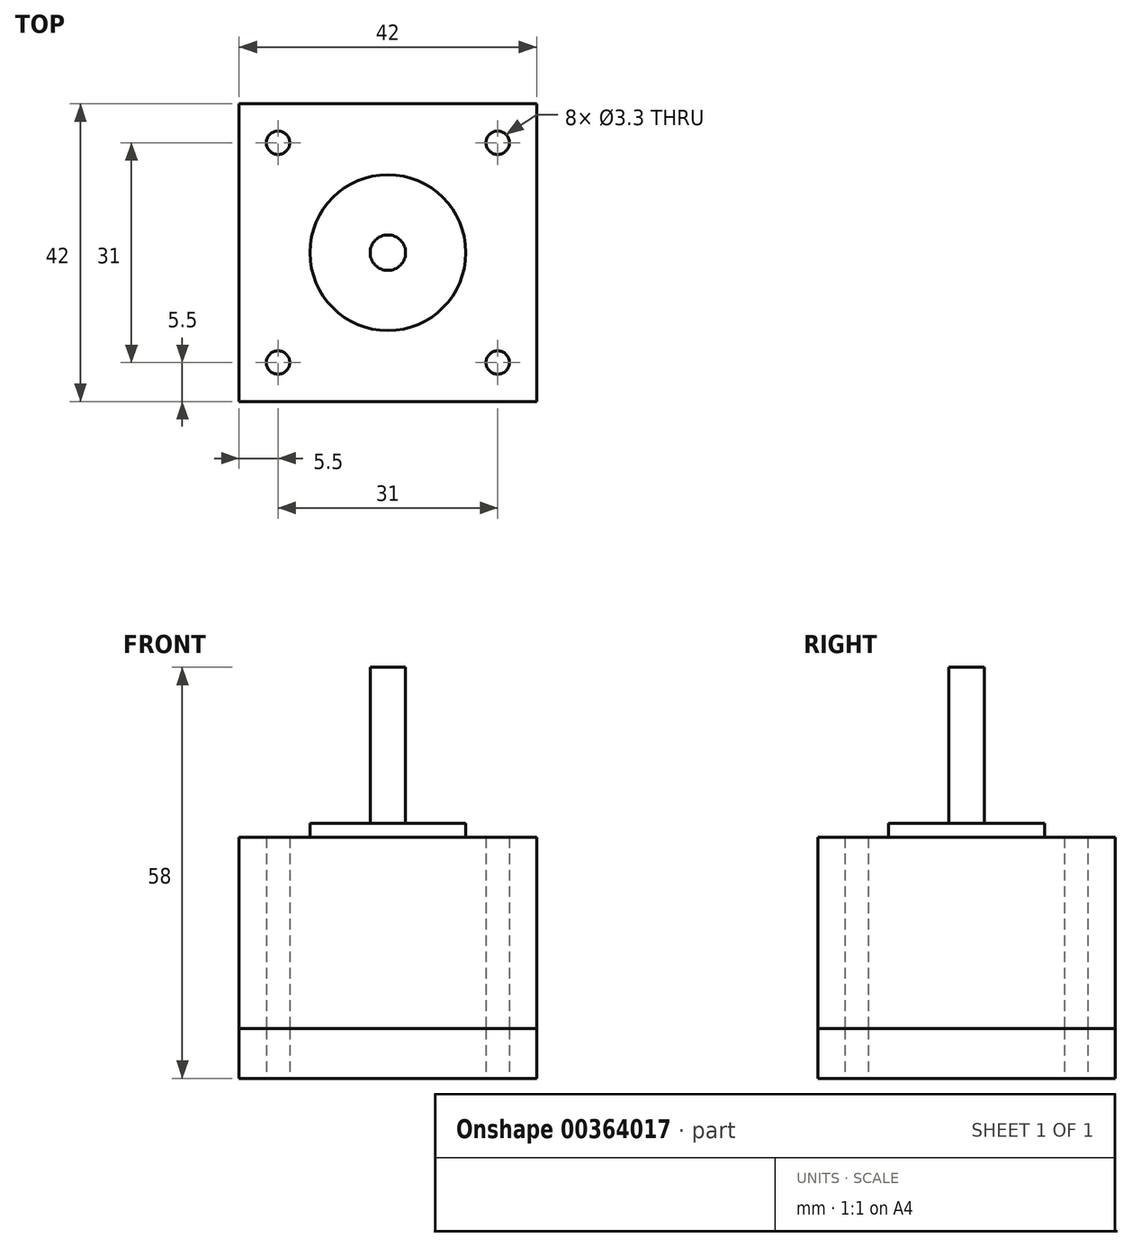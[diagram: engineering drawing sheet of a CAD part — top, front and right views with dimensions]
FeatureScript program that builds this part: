
annotation { "Feature Type Name" : "Feature", "Feature Type Description" : "" }
export const myFeature = defineFeature(function(context is Context, id is Id, definition is map)
    precondition{}
    {
        {
            var Q0;
            Q0=qCreatedBy(makeId("Top.planeOp"),FACE);
            var sketch = newSketch(context, id + "F0", { "sketchPlane" : qUnion([Q0])});
            skLineSegment(sketch, "E0.bottom", {"start": v(21, -21) * mm, "end": v(-21, -21) * mm});
            skLineSegment(sketch, "E0.top", {"start": v(21, 21) * mm, "end": v(-21, 21) * mm});
            skLineSegment(sketch, "E0.left", {"start": v(21, -21) * mm, "end": v(21, 21) * mm});
            skLineSegment(sketch, "E0.right", {"start": v(-21, -21) * mm, "end": v(-21, 21) * mm});
            skPoint(sketch, "E0.middle", {"position": v(0, 0) * mm});
            skSolve(sketch);
        }
        {
            var Q0;
            Q0=makeQuery(id+"F0.imprint","IMPRINT",FACE,{"disambiguationData":[TD([[makeQuery(id+"F0.imprint","IMPRINT",EDGE,{"derivedFrom":sQuery(id+"F0.wireOp",EDGE,"E0.bottom")}),-1.0]])]});
            extrude(context, id + "F1", {"entities" : qUnion([Q0]), "depth" : 7 * mm});
        }
        {
            var Q0;
            Q0=makeQuery(id+"F1.opExtrude","CAP_FACE",FACE,{"disambiguationData":[OSD([sQuery(id+"F0.wireOp",EDGE,"E0.bottom"),sQuery(id+"F0.wireOp",EDGE,"E0.top"),sQuery(id+"F0.wireOp",EDGE,"E0.left"),sQuery(id+"F0.wireOp",EDGE,"E0.right")])],"isStart":false});
            extrude(context, id + "F2", {"entities" : qUnion([Q0]), "depth" : 20 * mm});
        }
        {
            var Q0;
            Q0=makeQuery(id+"F2.opExtrude","CAP_FACE",FACE,{"disambiguationData":[OSD([sQuery(id+"F0.wireOp",EDGE,"E0.bottom"),sQuery(id+"F0.wireOp",EDGE,"E0.top"),sQuery(id+"F0.wireOp",EDGE,"E0.left"),sQuery(id+"F0.wireOp",EDGE,"E0.right")])],"isStart":false});
            extrude(context, id + "F3", {"entities" : qUnion([Q0]), "operationType" : NewBodyOperationType.ADD, "depth" : 7 * mm});
        }
        {
            var Q0;
            Q0=makeQuery(id+"F3.opExtrude","CAP_FACE",FACE,{"disambiguationData":[OSD([sQuery(id+"F0.wireOp",EDGE,"E0.bottom"),sQuery(id+"F0.wireOp",EDGE,"E0.top"),sQuery(id+"F0.wireOp",EDGE,"E0.left"),sQuery(id+"F0.wireOp",EDGE,"E0.right")])],"isStart":false});
            var sketch = newSketch(context, id + "F4", { "sketchPlane" : qUnion([Q0])});
            skPoint(sketch, "E1", {"position": v(-15.5, 15.5) * mm});
            skPoint(sketch, "E2.0.1.0", {"position": v(-15.5, -15.5) * mm});
            skPoint(sketch, "E2.1.0.0", {"position": v(15.5, 15.5) * mm});
            skPoint(sketch, "E2.1.1.0", {"position": v(15.5, -15.5) * mm});
            skLineSegment(sketch, "E2.direction1", {"start": v(-15.5, 15.5) * mm, "end": v(15.5, 15.5) * mm, "construction": true});
            skLineSegment(sketch, "E2.direction2", {"start": v(-15.5, 15.5) * mm, "end": v(-15.5, -15.5) * mm, "construction": true});
            skSolve(sketch);
        }
        {
            var Q0;
            Q0=sQuery(id+"F4.wireOp",VERTEX,"E1");
            var Q1;
            Q1=sQuery(id+"F4.wireOp",VERTEX,"E2.1.0.0");
            var Q2;
            Q2=sQuery(id+"F4.wireOp",VERTEX,"E2.0.1.0");
            var Q3;
            Q3=sQuery(id+"F4.wireOp",VERTEX,"E2.1.1.0");
            var Q4;
            Q4=makeQuery(id+"F1.opExtrude","SWEPT_BODY",BODY,{"disambiguationData":[OSD([sQuery(id+"F0.wireOp",EDGE,"E0.bottom"),sQuery(id+"F0.wireOp",EDGE,"E0.top"),sQuery(id+"F0.wireOp",EDGE,"E0.left"),sQuery(id+"F0.wireOp",EDGE,"E0.right")])]});
            var Q5;
            Q5=makeQuery(id+"F3.opExtrude","SWEPT_BODY",BODY,{"disambiguationData":[OSD([sQuery(id+"F0.wireOp",EDGE,"E0.bottom"),sQuery(id+"F0.wireOp",EDGE,"E0.top"),sQuery(id+"F0.wireOp",EDGE,"E0.left"),sQuery(id+"F0.wireOp",EDGE,"E0.right")])]});
            var Q6;
            Q6=makeQuery(id+"F2.opExtrude","SWEPT_BODY",BODY,{"disambiguationData":[OSD([sQuery(id+"F0.wireOp",EDGE,"E0.bottom"),sQuery(id+"F0.wireOp",EDGE,"E0.top"),sQuery(id+"F0.wireOp",EDGE,"E0.left"),sQuery(id+"F0.wireOp",EDGE,"E0.right")])]});
            hole(context, id + "F5", {"style" : HoleStyle.SIMPLE, "endStyle" : HoleEndStyle.THROUGH, "standardTappedOrClearance" : lookupTablePath({ "standard" : "ISO", "fit" : "Normal", "size" : "M3", "type" : "Clearance" }), "standardBlindInLast" : lookupTablePath({ "fit" : "Standard", "standard" : "ISO", "size" : "M3", "type" : "Clearance" }), "holeDiameter" : 3.3 * mm, "isTappedThrough" : true, "tappedDepth" : 12 * mm, "tapClearance" : 3, "locations" : qUnion([Q0, Q1, Q2, Q3]), "scope" : qUnion([Q4, Q5, Q6]), "startStyle" : HoleStartStyle.PART});
        }
        {
            var Q0;
            Q0=makeQuery(id+"F3.opExtrude","CAP_FACE",FACE,{"disambiguationData":[OSD([sQuery(id+"F0.wireOp",EDGE,"E0.bottom"),sQuery(id+"F0.wireOp",EDGE,"E0.top"),sQuery(id+"F0.wireOp",EDGE,"E0.left"),sQuery(id+"F0.wireOp",EDGE,"E0.right")])],"isStart":false});
            var sketch = newSketch(context, id + "F6", { "sketchPlane" : qUnion([Q0])});
            skCircle(sketch, "E3", {"center": v(0, 0) * mm, "radius": 11 * mm});
            skSolve(sketch);
        }
        {
            var Q0;
            Q0=makeQuery(id+"F6.imprint","IMPRINT",FACE,{"disambiguationData":[TD([[makeQuery(id+"F6.imprint","IMPRINT",EDGE,{"derivedFrom":sQuery(id+"F6.wireOp",EDGE,"E3")}),1.0]])]});
            extrude(context, id + "F7", {"entities" : qUnion([Q0]), "operationType" : NewBodyOperationType.ADD, "depth" : 2 * mm});
        }
        {
            var Q0;
            Q0=makeQuery(id+"F7.opExtrude","CAP_FACE",FACE,{"disambiguationData":[OSD([sQuery(id+"F6.wireOp",EDGE,"E3")])],"isStart":false});
            var sketch = newSketch(context, id + "F8", { "sketchPlane" : qUnion([Q0])});
            skCircle(sketch, "E4", {"center": v(0, 0) * mm, "radius": 2.5 * mm});
            skSolve(sketch);
        }
        {
            var Q0;
            Q0 = qSketchRegion(id + "F8", true);
            extrude(context, id + "F9", {"entities" : qUnion([Q0]), "operationType" : NewBodyOperationType.ADD, "depth" : 22 * mm});
        }
    });
